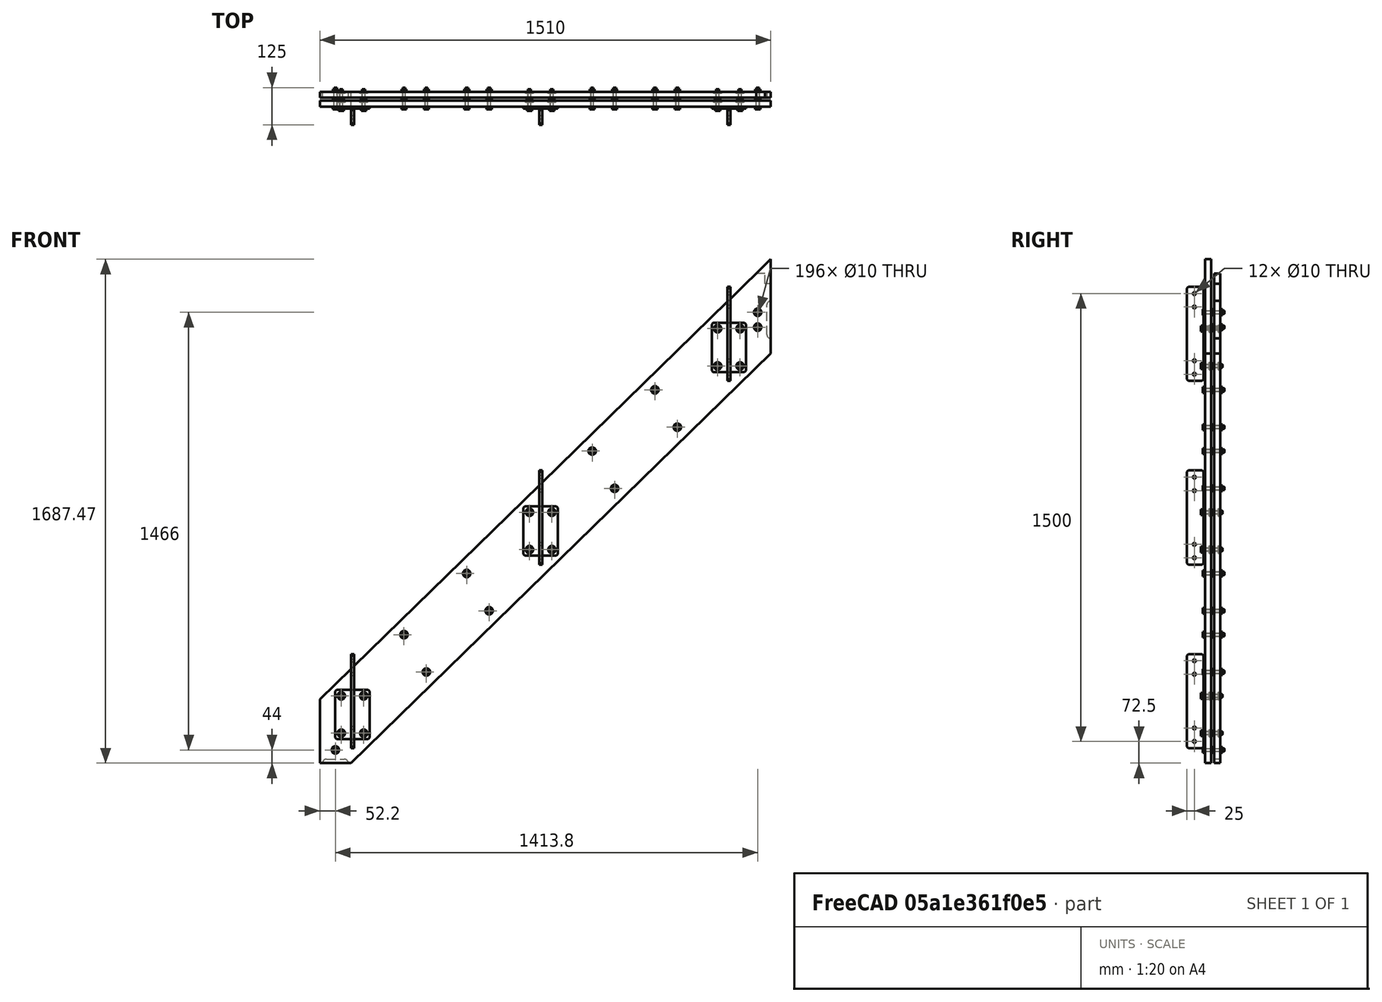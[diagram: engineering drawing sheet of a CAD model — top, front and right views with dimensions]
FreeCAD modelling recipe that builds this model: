
FCSTD DOCUMENT  (FreeCAD 0.17R10993 (Git))
Label: fasteners
License: All rights reserved
LicenseURL: http://en.wikipedia.org/wiki/All_rights_reserved
objects: Part::FeaturePython×11, Part::Extrusion×3, Part::Part2DObjectPython×2, Part::Feature×2, Part::Compound×2, Part::Cut×1
note: 21 computed .brp shape members not serialized (recipe doc carries the construction recipe); baked Part::Feature solids carry a one-line shape summary decoded from their .brp

FEATURE [Part::Part2DObjectPython] Circle003  # Draft 2D object (typed FeaturePython)
  FirstAngle = 0
  LastAngle = 0
  MakeFace = true
  Placement = pos=(32.2,-375,44) rot=(1,0,0;1.5708rad)
  Radius = 12.5
FEATURE [Part::Extrusion] Extrude002
  Base = -> Circle003
  Dir = (0,-1,0)
  DirMode = 0
  FaceMakerClass = Part::FaceMakerBullseye
  LengthFwd = 2
  LengthRev = 0
  Solid = false
  Symmetric = false
FEATURE [Part::Part2DObjectPython] Circle004  # Draft 2D object (typed FeaturePython)
  FirstAngle = 0
  LastAngle = 0
  MakeFace = true
  Placement = pos=(32.2,-375,44) rot=(1,0,0;1.5708rad)
  Radius = 5
FEATURE [Part::Extrusion] Extrude003
  Base = -> Circle004
  Dir = (0,-1,0)
  DirMode = 0
  FaceMakerClass = Part::FaceMakerBullseye
  LengthFwd = 2
  LengthRev = 0
  Solid = false
  Symmetric = false
FEATURE [Part::Cut] Cut002  label="washer"
  Base = -> Extrude002
  Tool = -> Extrude003
FEATURE [Part::Feature] BOLTS_part011_cs
  Placement = pos=(0,0,-2.5) rot=(0,0,1;0rad)
  shape: bbox 17 x 19.63 x 3e-07 mm, 0 faces, 0 solids (baked)
FEATURE [Part::Extrusion] Extrude004  label="nuts"
  Base = -> BOLTS_part011_cs
  Dir = (0,0,1)
  DirMode = 0
  FaceMakerClass = Part::FaceMakerBullseye
  LengthFwd = 6
  LengthRev = 0
  Placement = pos=(32.2,-347,44) rot=(1,0,0;1.5708rad)
  Solid = true
  Symmetric = false
FEATURE [Part::FeaturePython] Component  label="washer001"  # WARN: FeaturePython — macro-defined, semantics opaque (R4)
  CloneOf = -> Cut002
  HorizontalArea = 0
  MoveWithHost = false
  PerimeterLength = 0
  Placement = pos=(0,22,0) rot=(0,0,1;0rad)
  Role = 0
  VerticalArea = 0
FEATURE [Part::FeaturePython] Component001  label="washer002"  # WARN: FeaturePython — macro-defined, semantics opaque (R4)
  CloneOf = -> Cut002
  HorizontalArea = 0
  MoveWithHost = false
  PerimeterLength = 0
  Placement = pos=(0,30,0) rot=(0,0,1;0rad)
  Role = 0
  VerticalArea = 0
FEATURE [Part::FeaturePython] Component002  label="washer003"  # WARN: FeaturePython — macro-defined, semantics opaque (R4)
  CloneOf = -> Cut002
  HorizontalArea = 0
  MoveWithHost = false
  PerimeterLength = 0
  Placement = pos=(0,52,0) rot=(0,0,1;0rad)
  Role = 0
  VerticalArea = 0
FEATURE [Part::FeaturePython] Component003  label="nuts001"  # WARN: FeaturePython — macro-defined, semantics opaque (R4)
  CloneOf = -> Extrude004
  HorizontalArea = 0
  MoveWithHost = false
  PerimeterLength = 0
  Placement = pos=(32.2,-317,44) rot=(1,0,0;1.5708rad)
  Role = 0
  VerticalArea = 0
FEATURE [Part::Feature] BOLTS_part  label="Hexagon head bolt DIN 931 M10 - 66.0"
  Placement = pos=(32.2,-383.4,44) rot=(-1,0,0;1.5708rad)
  shape: bbox 17 x 72.4 x 19.63 mm, 11 faces (baked)
FEATURE [Part::Compound] Compound004  label="fastener_and_nuts"
  Links = -> [Cut002,Extrude004,Component003,Component,Component001,Component002,BOLTS_part]
FEATURE [Part::FeaturePython] Component004  label="fastener_and_nuts001"  # WARN: FeaturePython — macro-defined, semantics opaque (R4)
  CloneOf = -> Compound004
  HorizontalArea = 0
  MoveWithHost = false
  PerimeterLength = 0
  Placement = pos=(19.6902,3.33786e-06,56) rot=(0,0,1;0rad)
  Role = 0
  VerticalArea = 0
FEATURE [Part::FeaturePython] Array  # Draft array (typed FeaturePython)
  Angle = 360
  ArrayType = 0
  Axis = (0,0,1)
  Base = -> Component004
  Center = (0,0,0)
  Fuse = false
  IntervalAxis = (0,0,0)
  IntervalX = (75,0,0)
  IntervalY = (0,0,125)
  IntervalZ = (630,0,615)
  NumberPolar = 1
  NumberX = 2
  NumberY = 2
  NumberZ = 3
  Placement = pos=(0,-6,0) rot=(0,0,1;0rad)
FEATURE [Part::FeaturePython] Component005  label="fastener_and_nuts002"  # WARN: FeaturePython — macro-defined, semantics opaque (R4)
  CloneOf = -> Compound004
  HorizontalArea = 0
  MoveWithHost = false
  PerimeterLength = 0
  Placement = pos=(1413.8,0,1466) rot=(0,0,1;0rad)
  Role = 0
  VerticalArea = 0
FEATURE [Part::FeaturePython] Component006  label="fastener_and_nuts003"  # WARN: FeaturePython — macro-defined, semantics opaque (R4)
  CloneOf = -> Compound004
  HorizontalArea = 0
  MoveWithHost = false
  PerimeterLength = 0
  Placement = pos=(1413.8,0,1416) rot=(0,0,1;0rad)
  Role = 0
  VerticalArea = 0
FEATURE [Part::FeaturePython] double_beam_01  # a2plus imported part (geometry in sourceFile) (typed FeaturePython)
  fixedPosition = true
  sourceFile = double_beam.fcstd
  timeLastImport = 1.49424e+09
  updateColors = true
FEATURE [Part::FeaturePython] Array001  # Draft array (typed FeaturePython)
  Angle = 360
  ArrayType = 0
  Axis = (0,0,1)
  Base = -> Component004
  Center = (0,0,0)
  Fuse = false
  IntervalAxis = (0,0,0)
  IntervalX = (-75,0,125)
  IntervalY = (210,0,205)
  IntervalZ = (630,0,615)
  NumberPolar = 1
  NumberX = 2
  NumberY = 2
  NumberZ = 2
  Placement = pos=(285,0,205) rot=(0,0,1;0rad)
FEATURE [Part::Compound] Compound009  label="fasteners"
  Links = -> [Array,Compound004,Component005,Component006,Array001]
FEATURE [Part::FeaturePython] railing_plate_01  # a2plus imported part (geometry in sourceFile) (typed FeaturePython)
  fixedPosition = false
  sourceFile = railing_plate.fcstd
  timeLastImport = 1.49441e+09
  updateColors = true
